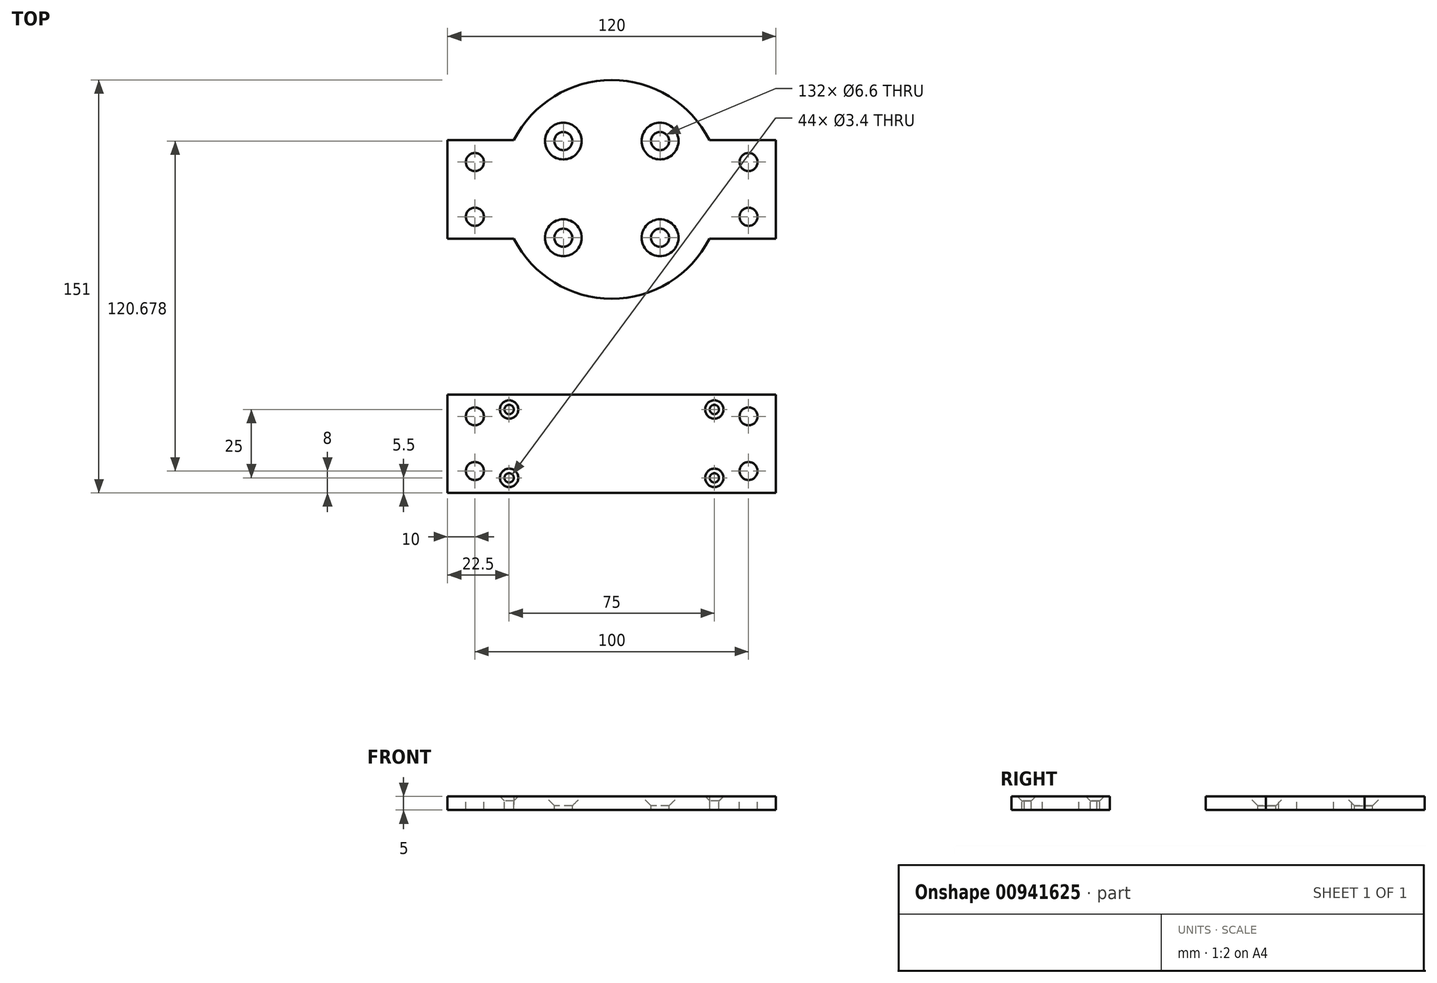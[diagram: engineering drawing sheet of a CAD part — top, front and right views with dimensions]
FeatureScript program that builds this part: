
annotation { "Feature Type Name" : "Feature", "Feature Type Description" : "" }
export const myFeature = defineFeature(function(context is Context, id is Id, definition is map)
    precondition{}
    {
        {
            var Q0;
            Q0=qCreatedBy(makeId("Top.planeOp"),FACE);
            var sketch = newSketch(context, id + "F0", { "sketchPlane" : qUnion([Q0])});
            skLineSegment(sketch, "E0", {"start": v(-43.1, 38.91) * mm, "end": v(-43.1, 38.91) * mm});
            skLineSegment(sketch, "E1", {"start": v(-60, 0) * mm, "end": v(-60, 18) * mm});
            skLineSegment(sketch, "E2", {"start": v(-60, 18) * mm, "end": v(-35.72, 18) * mm});
            skArc(sketch, "E3", {"start": v(35.72, 18) * mm, "mid": v(0, 40) * mm, "end": v(-35.72, 18) * mm});
            skLineSegment(sketch, "E4", {"start": v(35.72, 18) * mm, "end": v(60, 18) * mm});
            skLineSegment(sketch, "E5", {"start": v(60, 18) * mm, "end": v(60, 0) * mm});
            skLineSegment(sketch, "E6", {"start": v(0, 0) * mm, "end": v(90, 0) * mm, "construction": true});
            skLineSegment(sketch, "E7", {"start": v(0, 0) * mm, "end": v(-90, 0) * mm, "construction": true});
            skLineSegment(sketch, "E8.MirrorCS", {"start": v(-60, 0) * mm, "end": v(-60, -18) * mm});
            skLineSegment(sketch, "E9.MirrorCS", {"start": v(-60, -18) * mm, "end": v(-35.72, -18) * mm});
            skArc(sketch, "E10.MirrorCS", {"start": v(35.72, -18) * mm, "mid": v(0, -40) * mm, "end": v(-35.72, -18) * mm});
            skLineSegment(sketch, "E11.MirrorCS", {"start": v(35.72, -18) * mm, "end": v(60, -18) * mm});
            skLineSegment(sketch, "E12.MirrorCS", {"start": v(60, -18) * mm, "end": v(60, 0) * mm});
            skSolve(sketch);
        }
        {
            var Q0;
            Q0=makeQuery(id+"F0.imprint","IMPRINT",FACE,{"disambiguationData":[TD([[makeQuery(id+"F0.imprint","IMPRINT",EDGE,{"derivedFrom":sQuery(id+"F0.wireOp",EDGE,"E1")}),-1.0]])]});
            extrude(context, id + "F1", {"entities" : qUnion([Q0]), "depth" : 5 * mm, "offsetDistance" : 25 * mm});
        }
        {
            var Q0;
            Q0=makeQuery(id+"F1.opExtrude","CAP_FACE",FACE,{"disambiguationData":[OSD([sQuery(id+"F0.wireOp",EDGE,"E1"),sQuery(id+"F0.wireOp",EDGE,"E2"),sQuery(id+"F0.wireOp",EDGE,"E3"),sQuery(id+"F0.wireOp",EDGE,"E4"),sQuery(id+"F0.wireOp",EDGE,"E5"),sQuery(id+"F0.wireOp",EDGE,"E8.MirrorCS"),sQuery(id+"F0.wireOp",EDGE,"E9.MirrorCS"),sQuery(id+"F0.wireOp",EDGE,"E10.MirrorCS"),sQuery(id+"F0.wireOp",EDGE,"E11.MirrorCS"),sQuery(id+"F0.wireOp",EDGE,"E12.MirrorCS")])],"isStart":false});
            var sketch = newSketch(context, id + "F2", { "sketchPlane" : qUnion([Q0])});
            skCircle(sketch, "E13", {"center": v(0, 0) * mm, "radius": 25 * mm, "construction": true});
            skLineSegment(sketch, "E14", {"start": v(0, 0) * mm, "end": v(17.68, 17.68) * mm, "construction": true});
            skLineSegment(sketch, "E15", {"start": v(0, 0) * mm, "end": v(25, 0) * mm, "construction": true});
            skPoint(sketch, "E16", {"position": v(17.68, 17.68) * mm});
            skPoint(sketch, "E17.1.0", {"position": v(-17.68, 17.68) * mm});
            skPoint(sketch, "E17.2.0", {"position": v(-17.68, -17.68) * mm});
            skPoint(sketch, "E17.3.0", {"position": v(17.68, -17.68) * mm});
            skSolve(sketch);
        }
        {
            var Q0;
            Q0=sQuery(id+"F2.wireOp",VERTEX,"E17.1.0");
            var Q1;
            Q1=sQuery(id+"F2.wireOp",VERTEX,"E16");
            var Q2;
            Q2=sQuery(id+"F2.wireOp",VERTEX,"E17.3.0");
            var Q3;
            Q3=sQuery(id+"F2.wireOp",VERTEX,"E17.2.0");
            var Q4;
            Q4=makeQuery(id+"F1.opExtrude","SWEPT_BODY",BODY,{"disambiguationData":[OSD([sQuery(id+"F0.wireOp",EDGE,"E1"),sQuery(id+"F0.wireOp",EDGE,"E2"),sQuery(id+"F0.wireOp",EDGE,"E3"),sQuery(id+"F0.wireOp",EDGE,"E4"),sQuery(id+"F0.wireOp",EDGE,"E5"),sQuery(id+"F0.wireOp",EDGE,"E8.MirrorCS"),sQuery(id+"F0.wireOp",EDGE,"E9.MirrorCS"),sQuery(id+"F0.wireOp",EDGE,"E10.MirrorCS"),sQuery(id+"F0.wireOp",EDGE,"E11.MirrorCS"),sQuery(id+"F0.wireOp",EDGE,"E12.MirrorCS")])]});
            hole(context, id + "F3", {"style" : HoleStyle.C_SINK, "endStyle" : HoleEndStyle.THROUGH, "standardTappedOrClearance" : lookupTablePath({ "fit" : "Normal", "standard" : "ISO", "size" : "M6", "type" : "Clearance" }), "standardBlindInLast" : lookupTablePath({ "fit" : "Normal", "standard" : "ISO", "engagement" : "75%", "pitch" : "1 mm", "size" : "M6", "type" : "Clearance & tapped" }), "holeDiameter" : 6.6 * mm, "cSinkDiameter" : 13.44 * mm, "cSinkAngle" : 90 * degree, "majorDiameter" : 5 * mm, "isTappedThrough" : true, "tappedDepth" : 12 * mm, "tapClearance" : 3, "locations" : qUnion([Q0, Q1, Q2, Q3]), "scope" : qUnion([Q4])});
        }
        {
            var Q0;
            Q0=makeQuery(id+"F1.opExtrude","CAP_FACE",FACE,{"disambiguationData":[OSD([sQuery(id+"F0.wireOp",EDGE,"E1"),sQuery(id+"F0.wireOp",EDGE,"E2"),sQuery(id+"F0.wireOp",EDGE,"E3"),sQuery(id+"F0.wireOp",EDGE,"E4"),sQuery(id+"F0.wireOp",EDGE,"E5"),sQuery(id+"F0.wireOp",EDGE,"E8.MirrorCS"),sQuery(id+"F0.wireOp",EDGE,"E9.MirrorCS"),sQuery(id+"F0.wireOp",EDGE,"E10.MirrorCS"),sQuery(id+"F0.wireOp",EDGE,"E11.MirrorCS"),sQuery(id+"F0.wireOp",EDGE,"E12.MirrorCS")])],"isStart":false});
            var sketch = newSketch(context, id + "F4", { "sketchPlane" : qUnion([Q0])});
            skLineSegment(sketch, "E18.bottom", {"start": v(-50, 10) * mm, "end": v(50, 10) * mm, "construction": true});
            skLineSegment(sketch, "E18.top", {"start": v(-50, -10) * mm, "end": v(50, -10) * mm, "construction": true});
            skLineSegment(sketch, "E18.left", {"start": v(-50, 10) * mm, "end": v(-50, -10) * mm, "construction": true});
            skLineSegment(sketch, "E18.right", {"start": v(50, 10) * mm, "end": v(50, -10) * mm, "construction": true});
            skSolve(sketch);
        }
        {
            var Q0;
            Q0=sQuery(id+"F4.wireOp",VERTEX,"E18.bottom.start");
            var Q1;
            Q1=sQuery(id+"F4.wireOp",VERTEX,"E18.top.start");
            var Q2;
            Q2=sQuery(id+"F4.wireOp",VERTEX,"E18.top.end");
            var Q3;
            Q3=sQuery(id+"F4.wireOp",VERTEX,"E18.bottom.end");
            var Q4;
            Q4=makeQuery(id+"F1.opExtrude","SWEPT_BODY",BODY,{"disambiguationData":[OSD([sQuery(id+"F0.wireOp",EDGE,"E1"),sQuery(id+"F0.wireOp",EDGE,"E2"),sQuery(id+"F0.wireOp",EDGE,"E3"),sQuery(id+"F0.wireOp",EDGE,"E4"),sQuery(id+"F0.wireOp",EDGE,"E5"),sQuery(id+"F0.wireOp",EDGE,"E8.MirrorCS"),sQuery(id+"F0.wireOp",EDGE,"E9.MirrorCS"),sQuery(id+"F0.wireOp",EDGE,"E10.MirrorCS"),sQuery(id+"F0.wireOp",EDGE,"E11.MirrorCS"),sQuery(id+"F0.wireOp",EDGE,"E12.MirrorCS")])]});
            hole(context, id + "F5", {"style" : HoleStyle.SIMPLE, "endStyle" : HoleEndStyle.THROUGH, "standardTappedOrClearance" : lookupTablePath({ "fit" : "Normal", "standard" : "ISO", "size" : "M6", "type" : "Clearance" }), "standardBlindInLast" : lookupTablePath({ "fit" : "Normal", "standard" : "ISO", "engagement" : "75%", "pitch" : "1 mm", "size" : "M6", "type" : "Clearance & tapped" }), "holeDiameter" : 6.6 * mm, "majorDiameter" : 5 * mm, "isTappedThrough" : true, "tappedDepth" : 12 * mm, "tapClearance" : 3, "locations" : qUnion([Q0, Q1, Q2, Q3]), "scope" : qUnion([Q4])});
        }
        {
            var Q0;
            Q0=qCreatedBy(makeId("Top.planeOp"),FACE);
            var sketch = newSketch(context, id + "F6", { "sketchPlane" : qUnion([Q0])});
            skLineSegment(sketch, "E19.bottom", {"start": v(-60, -75) * mm, "end": v(60, -75) * mm});
            skLineSegment(sketch, "E19.top", {"start": v(-60, -111) * mm, "end": v(60, -111) * mm});
            skLineSegment(sketch, "E19.left", {"start": v(-60, -75) * mm, "end": v(-60, -111) * mm});
            skLineSegment(sketch, "E19.right", {"start": v(60, -75) * mm, "end": v(60, -111) * mm});
            skSolve(sketch);
        }
        {
            var Q0;
            Q0 = qSketchRegion(id + "F6", true);
            extrude(context, id + "F7", {"entities" : qUnion([Q0]), "depth" : 5 * mm, "offsetDistance" : 25 * mm});
        }
        {
            var Q0;
            Q0=makeQuery(id+"F7.opExtrude","CAP_FACE",FACE,{"disambiguationData":[OSD([sQuery(id+"F6.wireOp",EDGE,"E19.bottom"),sQuery(id+"F6.wireOp",EDGE,"E19.top"),sQuery(id+"F6.wireOp",EDGE,"E19.left"),sQuery(id+"F6.wireOp",EDGE,"E19.right")])],"isStart":false});
            var sketch = newSketch(context, id + "F8", { "sketchPlane" : qUnion([Q0])});
            skLineSegment(sketch, "E20.bottom", {"start": v(-37.5, -80.5) * mm, "end": v(37.5, -80.5) * mm, "construction": true});
            skLineSegment(sketch, "E20.top", {"start": v(-37.5, -105.5) * mm, "end": v(37.5, -105.5) * mm, "construction": true});
            skLineSegment(sketch, "E20.left", {"start": v(-37.5, -80.5) * mm, "end": v(-37.5, -105.5) * mm, "construction": true});
            skLineSegment(sketch, "E20.right", {"start": v(37.5, -80.5) * mm, "end": v(37.5, -105.5) * mm, "construction": true});
            skLineSegment(sketch, "E21", {"start": v(-60, -93) * mm, "end": v(60, -93) * mm, "construction": true});
            skPoint(sketch, "E22", {"position": v(-37.5, -93) * mm});
            skSolve(sketch);
        }
        {
            var Q0;
            Q0=sQuery(id+"F8.wireOp",VERTEX,"E20.bottom.start");
            var Q1;
            Q1=sQuery(id+"F8.wireOp",VERTEX,"E20.bottom.end");
            var Q2;
            Q2=sQuery(id+"F8.wireOp",VERTEX,"E20.top.end");
            var Q3;
            Q3=sQuery(id+"F8.wireOp",VERTEX,"E20.top.start");
            var Q4;
            Q4=makeQuery(id+"F7.opExtrude","SWEPT_BODY",BODY,{"disambiguationData":[OSD([sQuery(id+"F6.wireOp",EDGE,"E19.bottom"),sQuery(id+"F6.wireOp",EDGE,"E19.top"),sQuery(id+"F6.wireOp",EDGE,"E19.left"),sQuery(id+"F6.wireOp",EDGE,"E19.right")])]});
            hole(context, id + "F9", {"style" : HoleStyle.C_SINK, "endStyle" : HoleEndStyle.THROUGH, "standardTappedOrClearance" : lookupTablePath({ "fit" : "Normal", "standard" : "ISO", "size" : "M3", "type" : "Clearance" }), "standardBlindInLast" : lookupTablePath({ "fit" : "Normal", "standard" : "ISO", "engagement" : "75%", "pitch" : "0.5 mm", "size" : "M3", "type" : "Clearance & tapped" }), "holeDiameter" : 3.4 * mm, "cSinkDiameter" : 6.72 * mm, "cSinkAngle" : 90 * degree, "majorDiameter" : 3 * mm, "isTappedThrough" : true, "tappedDepth" : 12 * mm, "tapClearance" : 3, "locations" : qUnion([Q0, Q1, Q2, Q3]), "scope" : qUnion([Q4])});
        }
        {
            var Q0;
            Q0=makeQuery(id+"F7.opExtrude","CAP_FACE",FACE,{"disambiguationData":[OSD([sQuery(id+"F6.wireOp",EDGE,"E19.bottom"),sQuery(id+"F6.wireOp",EDGE,"E19.top"),sQuery(id+"F6.wireOp",EDGE,"E19.left"),sQuery(id+"F6.wireOp",EDGE,"E19.right")])],"isStart":false});
            var sketch = newSketch(context, id + "F10", { "sketchPlane" : qUnion([Q0])});
            skLineSegment(sketch, "E23.bottom", {"start": v(-50, -83) * mm, "end": v(50, -83) * mm, "construction": true});
            skLineSegment(sketch, "E23.top", {"start": v(-50, -103) * mm, "end": v(50, -103) * mm, "construction": true});
            skLineSegment(sketch, "E23.left", {"start": v(-50, -83) * mm, "end": v(-50, -103) * mm, "construction": true});
            skLineSegment(sketch, "E23.right", {"start": v(50, -83) * mm, "end": v(50, -103) * mm, "construction": true});
            skLineSegment(sketch, "E24", {"start": v(-60, -93) * mm, "end": v(60, -93) * mm, "construction": true});
            skPoint(sketch, "E25", {"position": v(-50, -93) * mm});
            skSolve(sketch);
        }
        {
            var Q0;
            Q0=sQuery(id+"F10.wireOp",VERTEX,"E23.bottom.start");
            var Q1;
            Q1=sQuery(id+"F10.wireOp",VERTEX,"E23.top.start");
            var Q2;
            Q2=sQuery(id+"F10.wireOp",VERTEX,"E23.bottom.end");
            var Q3;
            Q3=sQuery(id+"F10.wireOp",VERTEX,"E23.top.end");
            var Q4;
            Q4=makeQuery(id+"F7.opExtrude","SWEPT_BODY",BODY,{"disambiguationData":[OSD([sQuery(id+"F6.wireOp",EDGE,"E19.bottom"),sQuery(id+"F6.wireOp",EDGE,"E19.top"),sQuery(id+"F6.wireOp",EDGE,"E19.left"),sQuery(id+"F6.wireOp",EDGE,"E19.right")])]});
            hole(context, id + "F11", {"style" : HoleStyle.SIMPLE, "endStyle" : HoleEndStyle.THROUGH, "standardTappedOrClearance" : lookupTablePath({ "fit" : "Normal", "standard" : "ISO", "size" : "M6", "type" : "Clearance" }), "standardBlindInLast" : lookupTablePath({ "fit" : "Normal", "standard" : "ISO", "engagement" : "75%", "pitch" : "1 mm", "size" : "M6", "type" : "Clearance & tapped" }), "holeDiameter" : 6.6 * mm, "majorDiameter" : 5 * mm, "isTappedThrough" : true, "tappedDepth" : 12 * mm, "tapClearance" : 3, "locations" : qUnion([Q0, Q1, Q2, Q3]), "scope" : qUnion([Q4])});
        }
    });
